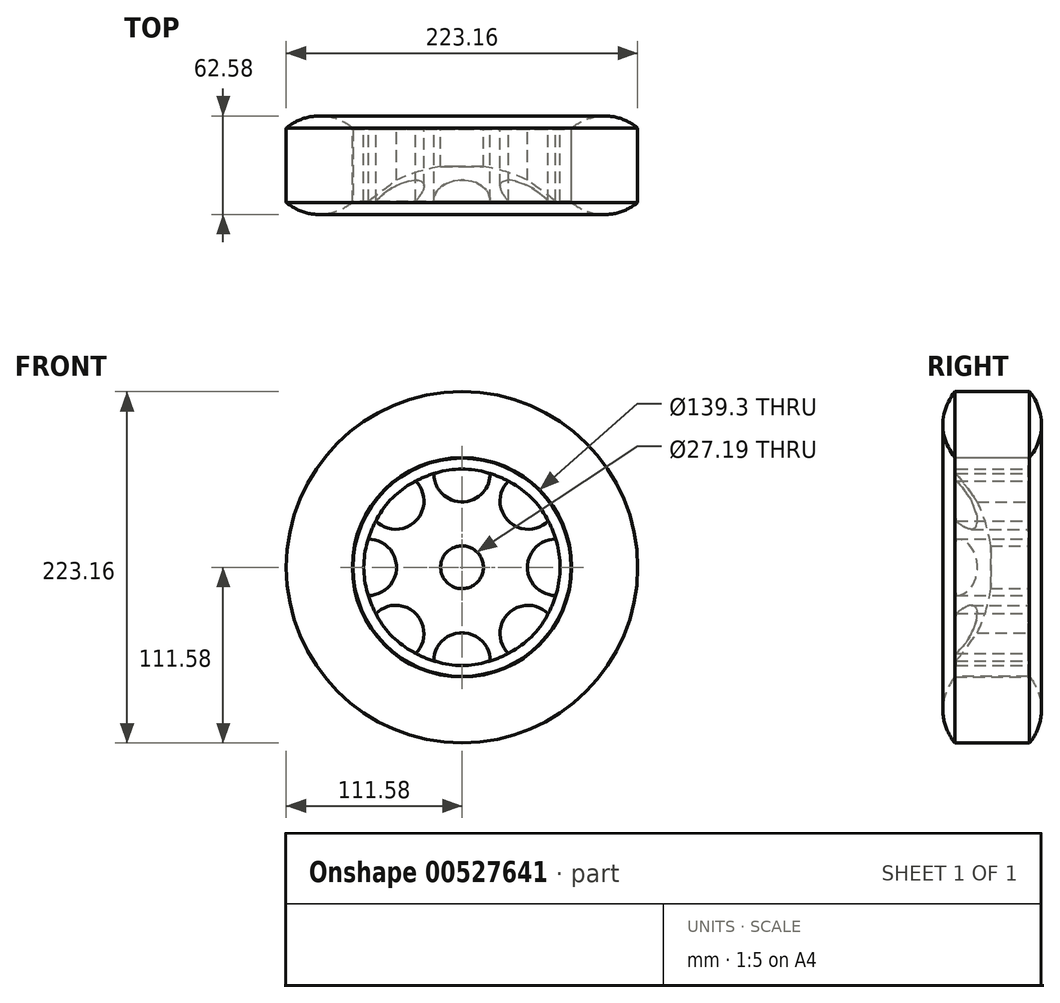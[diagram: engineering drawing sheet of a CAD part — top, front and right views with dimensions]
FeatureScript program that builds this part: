
annotation { "Feature Type Name" : "Feature", "Feature Type Description" : "" }
export const myFeature = defineFeature(function(context is Context, id is Id, definition is map)
    precondition{}
    {
        {
            var Q0;
            Q0=qCreatedBy(makeId("Right.planeOp"),FACE);
            var sketch = newSketch(context, id + "F0", { "sketchPlane" : qUnion([Q0])});
            skLineSegment(sketch, "E0.left", {"start": v(22.95, 0) * mm, "end": v(22.95, 62.13) * mm});
            skPoint(sketch, "E0.middle", {"position": v(0, 0) * mm});
            skArc(sketch, "E1", {"start": v(0, 0) * mm, "mid": v(-5.92, 33.12) * mm, "end": v(-22.95, 62.13) * mm});
            skLineSegment(sketch, "E2.left", {"start": v(-22.95, 62.13) * mm, "end": v(-22.95, 62.13) * mm});
            skLineSegment(sketch, "E2.right", {"start": v(22.95, 62.13) * mm, "end": v(22.95, 62.13) * mm});
            skLineSegment(sketch, "E3.top", {"start": v(22.95, 69.28) * mm, "end": v(-22.95, 69.28) * mm});
            skLineSegment(sketch, "E3.left", {"start": v(22.95, 62.13) * mm, "end": v(22.95, 69.28) * mm});
            skLineSegment(sketch, "E3.right", {"start": v(-22.95, 62.13) * mm, "end": v(-22.95, 69.28) * mm});
            skLineSegment(sketch, "E4", {"start": v(0, 0) * mm, "end": v(22.95, 0) * mm});
            skPoint(sketch, "E0.bottom.end.orphan", {"position": v(-22.95, -62.13) * mm});
            skPoint(sketch, "E0.bottom.start.orphan", {"position": v(22.95, -62.13) * mm});
            skSolve(sketch);
        }
        {
            var Q0;
            Q0=makeQuery(id+"F0.imprint","IMPRINT",FACE,{"disambiguationData":[TD([[makeQuery(id+"F0.imprint","IMPRINT",EDGE,{"derivedFrom":sQuery(id+"F0.wireOp",EDGE,"E0.left")}),1.0]])]});
            var Q1;
            Q1=sQuery(id+"F0.wireOp",EDGE,"E4");
            revolve(context, id + "F1", {"entities" : qUnion([Q0]), "axis" : qUnion([Q1]), "revolveType" : RevolveType.FULL});
        }
        {
            var Q0;
            Q0=qCreatedBy(makeId("Front.planeOp"),FACE);
            var sketch = newSketch(context, id + "F2", { "sketchPlane" : qUnion([Q0])});
            skPoint(sketch, "E5.middle", {"position": v(0, 76.73) * mm});
            skArc(sketch, "E6", {"start": v(-17.88, 59.45) * mm, "mid": v(0, 41.57) * mm, "end": v(17.88, 59.45) * mm});
            skArc(sketch, "E7", {"start": v(17.88, 59.45) * mm, "mid": v(0, 62.38) * mm, "end": v(-17.88, 59.45) * mm});
            skPoint(sketch, "E5.top.end.orphan", {"position": v(-17.88, 94.02) * mm});
            skPoint(sketch, "E5.top.start.orphan", {"position": v(17.88, 94.02) * mm});
            skArc(sketch, "E8.1.0", {"start": v(-54.68, 29.4) * mm, "mid": v(-29.4, 29.4) * mm, "end": v(-29.4, 54.68) * mm});
            skArc(sketch, "E8.1.1", {"start": v(-29.4, 54.68) * mm, "mid": v(-44.1, 44.1) * mm, "end": v(-54.68, 29.4) * mm});
            skArc(sketch, "E8.2.0", {"start": v(-59.45, -17.88) * mm, "mid": v(-41.57, 0) * mm, "end": v(-59.45, 17.88) * mm});
            skArc(sketch, "E8.2.1", {"start": v(-59.45, 17.88) * mm, "mid": v(-62.38, 0) * mm, "end": v(-59.45, -17.88) * mm});
            skArc(sketch, "E8.3.0", {"start": v(-29.4, -54.68) * mm, "mid": v(-29.4, -29.4) * mm, "end": v(-54.68, -29.4) * mm});
            skArc(sketch, "E8.3.1", {"start": v(-54.68, -29.4) * mm, "mid": v(-44.1, -44.1) * mm, "end": v(-29.4, -54.68) * mm});
            skArc(sketch, "E8.4.0", {"start": v(17.88, -59.45) * mm, "mid": v(0, -41.57) * mm, "end": v(-17.88, -59.45) * mm});
            skArc(sketch, "E8.4.1", {"start": v(-17.88, -59.45) * mm, "mid": v(0, -62.38) * mm, "end": v(17.88, -59.45) * mm});
            skArc(sketch, "E8.5.0", {"start": v(54.68, -29.4) * mm, "mid": v(29.4, -29.4) * mm, "end": v(29.4, -54.68) * mm});
            skArc(sketch, "E8.5.1", {"start": v(29.4, -54.68) * mm, "mid": v(44.1, -44.1) * mm, "end": v(54.68, -29.4) * mm});
            skArc(sketch, "E8.6.0", {"start": v(59.45, 17.88) * mm, "mid": v(41.57, 0) * mm, "end": v(59.45, -17.88) * mm});
            skArc(sketch, "E8.6.1", {"start": v(59.45, -17.88) * mm, "mid": v(62.38, 0) * mm, "end": v(59.45, 17.88) * mm});
            skArc(sketch, "E8.7.0", {"start": v(29.4, 54.68) * mm, "mid": v(29.4, 29.4) * mm, "end": v(54.68, 29.4) * mm});
            skArc(sketch, "E8.7.1", {"start": v(54.68, 29.4) * mm, "mid": v(44.1, 44.1) * mm, "end": v(29.4, 54.68) * mm});
            skPoint(sketch, "E8.center", {"position": v(0, 0) * mm});
            skCircle(sketch, "E9", {"center": v(0, 0) * mm, "radius": 13.6 * mm});
            skSolve(sketch);
        }
        {
            var Q0;
            Q0=makeQuery(id+"F2.imprint","IMPRINT",FACE,{"disambiguationData":[TD([[makeQuery(id+"F2.imprint","IMPRINT",EDGE,{"derivedFrom":sQuery(id+"F2.wireOp",EDGE,"E8.1.0")}),1.0]])]});
            var Q1;
            Q1=makeQuery(id+"F2.imprint","IMPRINT",FACE,{"disambiguationData":[TD([[makeQuery(id+"F2.imprint","IMPRINT",EDGE,{"derivedFrom":sQuery(id+"F2.wireOp",EDGE,"E6")}),1.0]])]});
            var Q2;
            Q2=makeQuery(id+"F2.imprint","IMPRINT",FACE,{"disambiguationData":[TD([[makeQuery(id+"F2.imprint","IMPRINT",EDGE,{"derivedFrom":sQuery(id+"F2.wireOp",EDGE,"E8.7.0")}),1.0]])]});
            var Q3;
            Q3=makeQuery(id+"F2.imprint","IMPRINT",FACE,{"disambiguationData":[TD([[makeQuery(id+"F2.imprint","IMPRINT",EDGE,{"derivedFrom":sQuery(id+"F2.wireOp",EDGE,"E8.6.0")}),1.0]])]});
            var Q4;
            Q4=makeQuery(id+"F2.imprint","IMPRINT",FACE,{"disambiguationData":[TD([[makeQuery(id+"F2.imprint","IMPRINT",EDGE,{"derivedFrom":sQuery(id+"F2.wireOp",EDGE,"E8.5.0")}),1.0]])]});
            var Q5;
            Q5=makeQuery(id+"F2.imprint","IMPRINT",FACE,{"disambiguationData":[TD([[makeQuery(id+"F2.imprint","IMPRINT",EDGE,{"derivedFrom":sQuery(id+"F2.wireOp",EDGE,"E8.4.0")}),1.0]])]});
            var Q6;
            Q6=makeQuery(id+"F2.imprint","IMPRINT",FACE,{"disambiguationData":[TD([[makeQuery(id+"F2.imprint","IMPRINT",EDGE,{"derivedFrom":sQuery(id+"F2.wireOp",EDGE,"E8.3.0")}),1.0]])]});
            var Q7;
            Q7=makeQuery(id+"F2.imprint","IMPRINT",FACE,{"disambiguationData":[TD([[makeQuery(id+"F2.imprint","IMPRINT",EDGE,{"derivedFrom":sQuery(id+"F2.wireOp",EDGE,"E8.2.0")}),1.0]])]});
            extrude(context, id + "F3", {"entities" : qUnion([Q0, Q1, Q2, Q3, Q4, Q5, Q6, Q7]), "operationType" : NewBodyOperationType.REMOVE, "endBound" : BoundingType.SYMMETRIC, "depth" : 98.55 * mm, "offsetDistance" : 25.4 * mm});
        }
        {
            var Q0;
            Q0=makeQuery(id+"F2.imprint","IMPRINT",FACE,{"disambiguationData":[TD([[makeQuery(id+"F2.imprint","IMPRINT",EDGE,{"derivedFrom":sQuery(id+"F2.wireOp",EDGE,"E9")}),1.0]])]});
            extrude(context, id + "F4", {"entities" : qUnion([Q0]), "operationType" : NewBodyOperationType.REMOVE, "endBound" : BoundingType.SYMMETRIC, "depth" : 82.8 * mm, "offsetDistance" : 25.4 * mm});
        }
        {
            var Q0;
            Q0=qCreatedBy(makeId("Right.planeOp"),FACE);
            var sketch = newSketch(context, id + "F5", { "sketchPlane" : qUnion([Q0])});
            skLineSegment(sketch, "E10.bottom", {"start": v(23.63, 69.65) * mm, "end": v(-23.63, 69.65) * mm});
            skLineSegment(sketch, "E10.top", {"start": v(23.63, 111.58) * mm, "end": v(-23.63, 111.58) * mm});
            skLineSegment(sketch, "E10.left", {"start": v(23.63, 69.65) * mm, "end": v(23.63, 111.58) * mm});
            skLineSegment(sketch, "E10.right", {"start": v(-23.63, 69.65) * mm, "end": v(-23.63, 111.58) * mm});
            skPoint(sketch, "E10.middle", {"position": v(0, 90.62) * mm});
            skArc(sketch, "E11", {"start": v(-23.63, 111.58) * mm, "mid": v(-31.29, 90.62) * mm, "end": v(-23.63, 69.65) * mm});
            skLineSegment(sketch, "E12", {"start": v(0, 111.58) * mm, "end": v(0, 134.55) * mm});
            skPoint(sketch, "E12.endSnap0", {"position": v(0, 111.58) * mm});
            skArc(sketch, "E13.MirrorCS", {"start": v(23.63, 111.58) * mm, "mid": v(31.29, 90.62) * mm, "end": v(23.63, 69.65) * mm});
            skLineSegment(sketch, "E14", {"start": v(-28.02, 0) * mm, "end": v(-71.7, 0) * mm});
            skSolve(sketch);
        }
        {
            var Q0;
            Q0=makeQuery(id+"F5.imprint","IMPRINT",FACE,{"disambiguationData":[TD([[makeQuery(id+"F5.imprint","IMPRINT",EDGE,{"derivedFrom":sQuery(id+"F5.wireOp",EDGE,"E10.bottom")}),-1.0]])]});
            var Q1;
            Q1=makeQuery(id+"F5.imprint","IMPRINT",FACE,{"disambiguationData":[TD([[makeQuery(id+"F5.imprint","IMPRINT",EDGE,{"derivedFrom":sQuery(id+"F5.wireOp",EDGE,"E10.left")}),-1.0]])]});
            var Q2;
            Q2=makeQuery(id+"F5.imprint","IMPRINT",FACE,{"disambiguationData":[TD([[makeQuery(id+"F5.imprint","IMPRINT",EDGE,{"derivedFrom":sQuery(id+"F5.wireOp",EDGE,"E10.right")}),1.0]])]});
            var Q3;
            Q3=sQuery(id+"F5.wireOp",EDGE,"E14");
            revolve(context, id + "F6", {"entities" : qUnion([Q0, Q1, Q2]), "axis" : qUnion([Q3]), "revolveType" : RevolveType.FULL});
        }
    });
